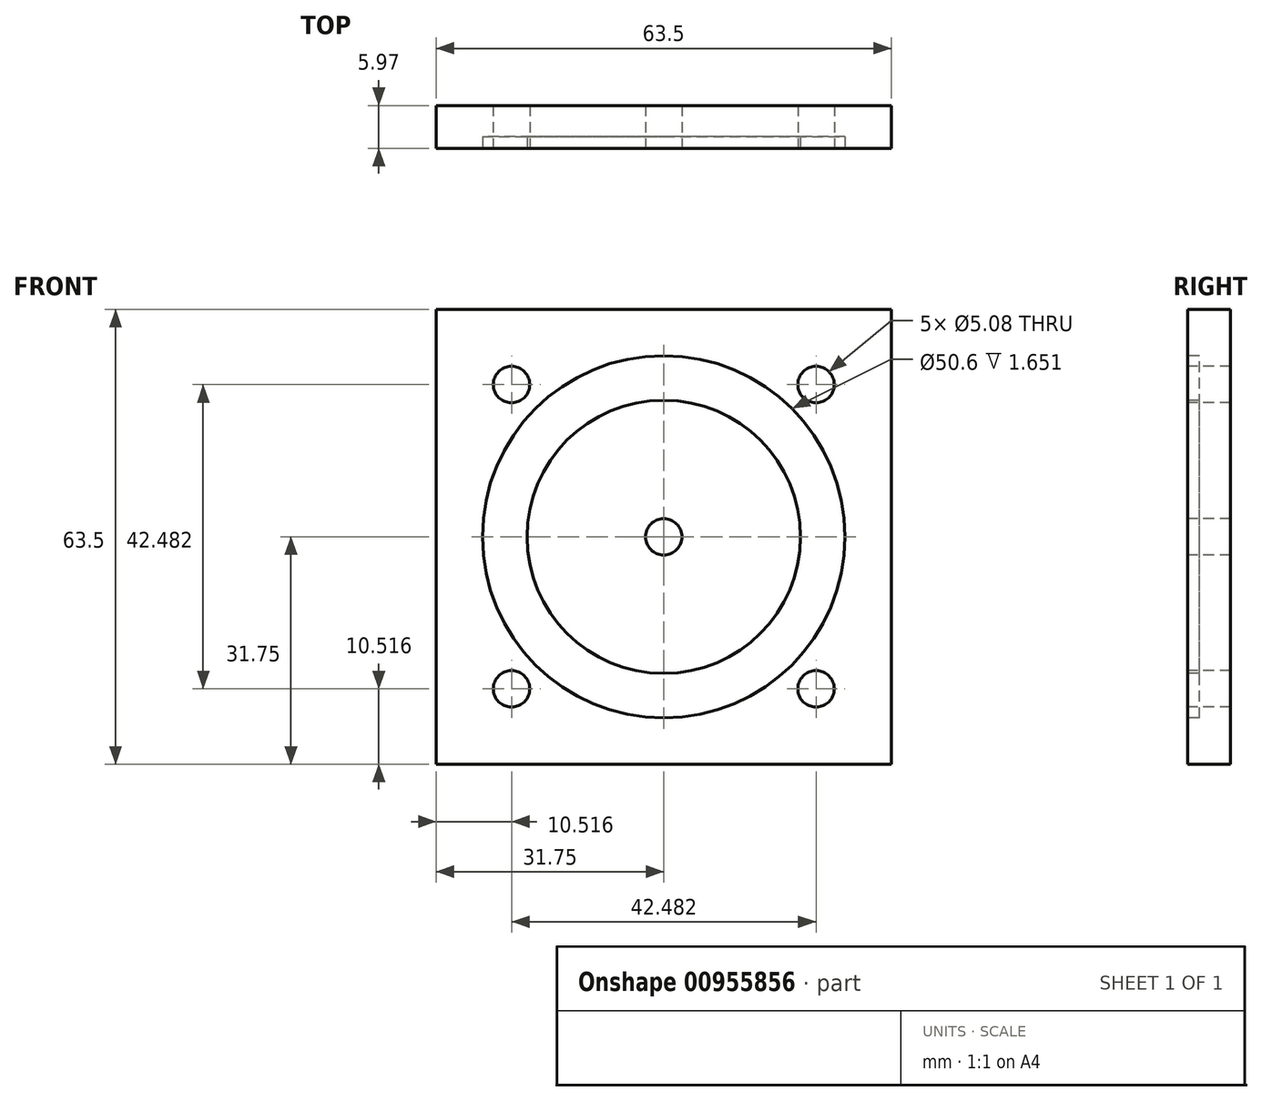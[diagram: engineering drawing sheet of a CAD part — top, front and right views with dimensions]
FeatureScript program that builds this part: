
annotation { "Feature Type Name" : "Feature", "Feature Type Description" : "" }
export const myFeature = defineFeature(function(context is Context, id is Id, definition is map)
    precondition{}
    {
        {
            var Q0;
            Q0=qCreatedBy(makeId("Front.planeOp"),FACE);
            var sketch = newSketch(context, id + "F0", { "sketchPlane" : qUnion([Q0])});
            skLineSegment(sketch, "E0.bottom", {"start": v(0, 0) * mm, "end": v(63.5, 0) * mm});
            skLineSegment(sketch, "E0.top", {"start": v(0, 63.5) * mm, "end": v(63.5, 63.5) * mm});
            skLineSegment(sketch, "E0.left", {"start": v(0, 0) * mm, "end": v(0, 63.5) * mm});
            skLineSegment(sketch, "E0.right", {"start": v(63.5, 0) * mm, "end": v(63.5, 63.5) * mm});
            skPoint(sketch, "E1", {"position": v(10.52, 53) * mm});
            skPoint(sketch, "E2", {"position": v(10.52, 10.52) * mm});
            skPoint(sketch, "E3", {"position": v(53, 10.52) * mm});
            skPoint(sketch, "E4", {"position": v(53, 53) * mm});
            skPoint(sketch, "E5", {"position": v(31.75, 31.75) * mm});
            skCircle(sketch, "E6", {"center": v(31.75, 31.75) * mm, "radius": 25.3 * mm});
            skCircle(sketch, "E7", {"center": v(31.75, 31.75) * mm, "radius": 19.08 * mm});
            skSolve(sketch);
        }
        {
            var Q0;
            Q0=makeQuery(id+"F0.imprint","IMPRINT",FACE,{"disambiguationData":[TD([[makeQuery(id+"F0.imprint","IMPRINT",EDGE,{"derivedFrom":sQuery(id+"F0.wireOp",EDGE,"E0.bottom")}),1.0]])]});
            var Q1;
            Q1=makeQuery(id+"F0.imprint","IMPRINT",FACE,{"disambiguationData":[TD([[makeQuery(id+"F0.imprint","IMPRINT",EDGE,{"derivedFrom":sQuery(id+"F0.wireOp",EDGE,"E7")}),1.0]])]});
            var Q2;
            Q2=makeQuery(id+"F0.imprint","IMPRINT",FACE,{"disambiguationData":[TD([[makeQuery(id+"F0.imprint","IMPRINT",EDGE,{"derivedFrom":sQuery(id+"F0.wireOp",EDGE,"E6")}),1.0]])]});
            extrude(context, id + "F1", {"entities" : qUnion([Q0, Q1, Q2]), "depth" : 5.97 * mm, "offsetDistance" : 25.4 * mm});
        }
        {
            var Q0;
            Q0=makeQuery(id+"F1.opExtrude","CAP_FACE",FACE,{"disambiguationData":[OSD([sQuery(id+"F0.wireOp",EDGE,"E0.bottom"),sQuery(id+"F0.wireOp",EDGE,"E0.top"),sQuery(id+"F0.wireOp",EDGE,"E0.left"),sQuery(id+"F0.wireOp",EDGE,"E0.right")])],"isStart":false});
            var sketch = newSketch(context, id + "F2", { "sketchPlane" : qUnion([Q0])});
            skSolve(sketch);
        }
        {
            var Q0;
            Q0=makeQuery(id+"F2.imprint","IMPRINT",FACE,{"disambiguationData":[TD([[makeQuery(id+"F2.imprint","IMPRINT",EDGE,{"derivedFrom":makeQuery(id+"F1.opExtrude","CAP_EDGE",EDGE,{"disambiguationData":[OSD([sQuery(id+"F0.wireOp",EDGE,"E0.bottom")])],"isStart":false})}),1.0]])]});
            var sketch = newSketch(context, id + "F3", { "sketchPlane" : qUnion([Q0])});
            skCircle(sketch, "E8", {"center": v(31.75, 31.75) * mm, "radius": 25.3 * mm});
            skCircle(sketch, "E9", {"center": v(31.75, 31.75) * mm, "radius": 19.08 * mm});
            skSolve(sketch);
        }
        {
            var Q0;
            Q0=makeQuery(id+"F3.imprint","IMPRINT",FACE,{"disambiguationData":[TD([[makeQuery(id+"F3.imprint","IMPRINT",EDGE,{"derivedFrom":sQuery(id+"F3.wireOp",EDGE,"E8")}),1.0]])]});
            extrude(context, id + "F4", {"entities" : qUnion([Q0]), "operationType" : NewBodyOperationType.REMOVE, "oppositeDirection" : true, "depth" : 1.65 * mm, "offsetDistance" : 25.4 * mm});
        }
        {
            var Q0;
            Q0=sQuery(id+"F0.wireOp",VERTEX,"E1");
            var Q1;
            Q1=sQuery(id+"F0.wireOp",VERTEX,"E4");
            var Q2;
            Q2=sQuery(id+"F0.wireOp",VERTEX,"E2");
            var Q3;
            Q3=sQuery(id+"F0.wireOp",VERTEX,"E3");
            var Q4;
            Q4=sQuery(id+"F0.wireOp",VERTEX,"E5");
            var Q5;
            Q5=makeQuery(id+"F1.opExtrude","SWEPT_BODY",BODY,{"disambiguationData":[OSD([sQuery(id+"F0.wireOp",EDGE,"E0.bottom"),sQuery(id+"F0.wireOp",EDGE,"E0.top"),sQuery(id+"F0.wireOp",EDGE,"E0.left"),sQuery(id+"F0.wireOp",EDGE,"E0.right")])]});
            hole(context, id + "F5", {"style" : HoleStyle.SIMPLE, "endStyle" : HoleEndStyle.THROUGH, "oppositeDirection" : true, "holeDiameter" : 5.08 * mm, "majorDiameter" : 6.35 * mm, "isTappedThrough" : true, "tappedDepth" : 12.7 * mm, "tapClearance" : 3, "locations" : qUnion([Q0, Q1, Q2, Q3, Q4]), "scope" : qUnion([Q5]), "startStyle" : HoleStartStyle.SKETCH});
        }
    });
